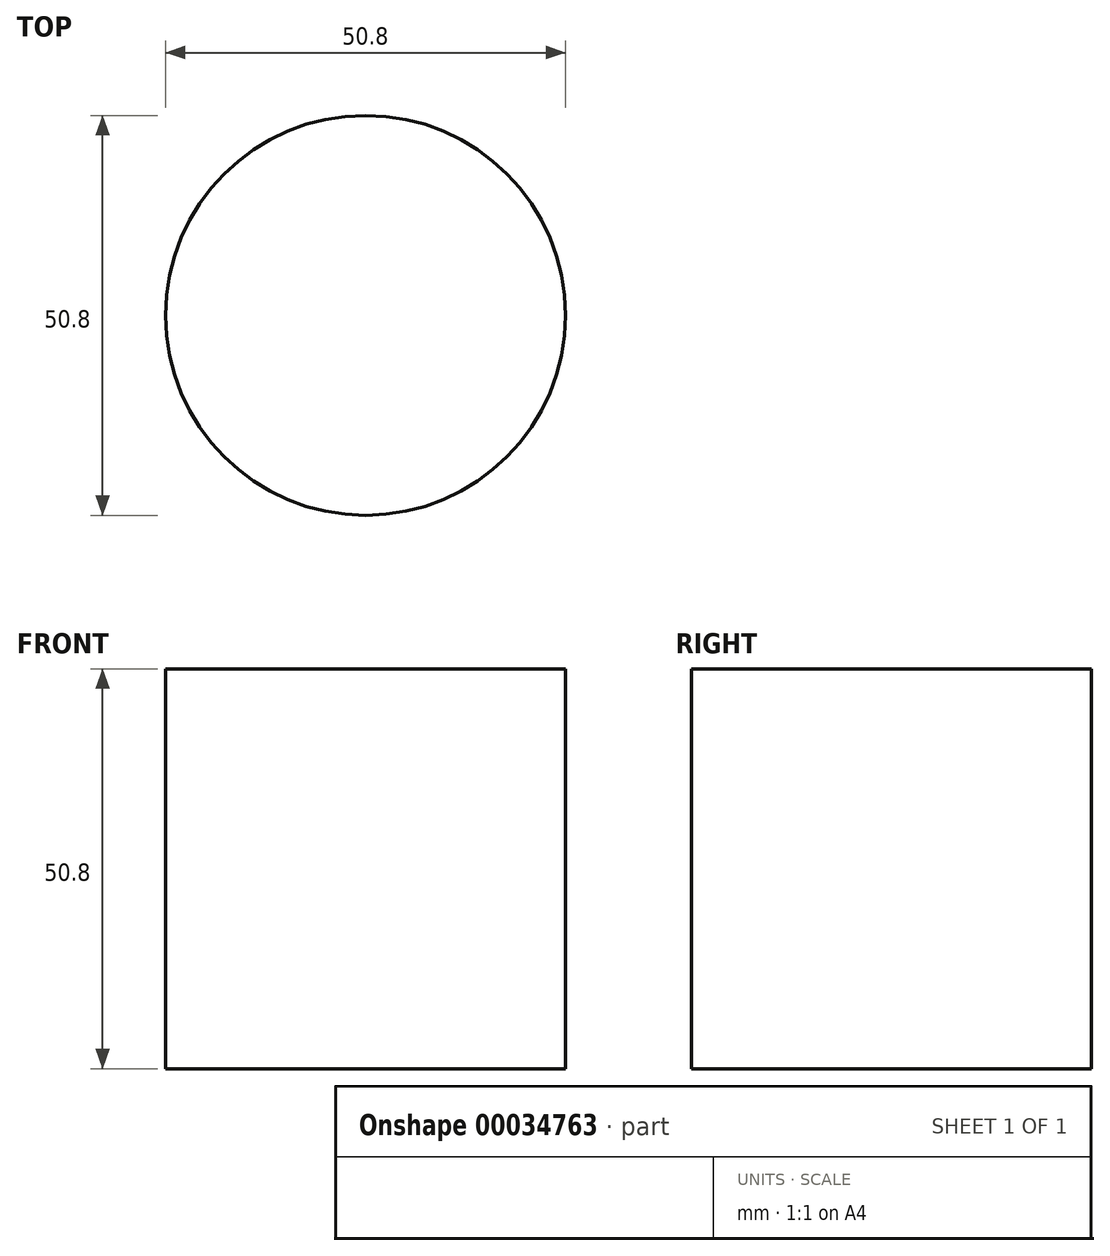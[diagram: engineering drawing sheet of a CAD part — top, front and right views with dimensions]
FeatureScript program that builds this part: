
annotation { "Feature Type Name" : "Feature", "Feature Type Description" : "" }
export const myFeature = defineFeature(function(context is Context, id is Id, definition is map)
    precondition{}
    {
        {
            var Q0;
            Q0=qCreatedBy(makeId("Top.planeOp"),FACE);
            var sketch = newSketch(context, id + "F0", { "sketchPlane" : qUnion([Q0])});
            skCircle(sketch, "E0", {"center": v(0, 0) * mm, "radius": 25.4 * mm});
            skSolve(sketch);
        }
        {
            var Q0;
            Q0=makeQuery(id+"F0.imprint","IMPRINT",FACE,{"disambiguationData":[TD([[makeQuery(id+"F0.imprint","IMPRINT",EDGE,{"derivedFrom":sQuery(id+"F0.wireOp",EDGE,"E0")}),1.0]])]});
            extrude(context, id + "F1", {"entities" : qUnion([Q0]), "depth" : 50.8 * mm});
        }
    });
